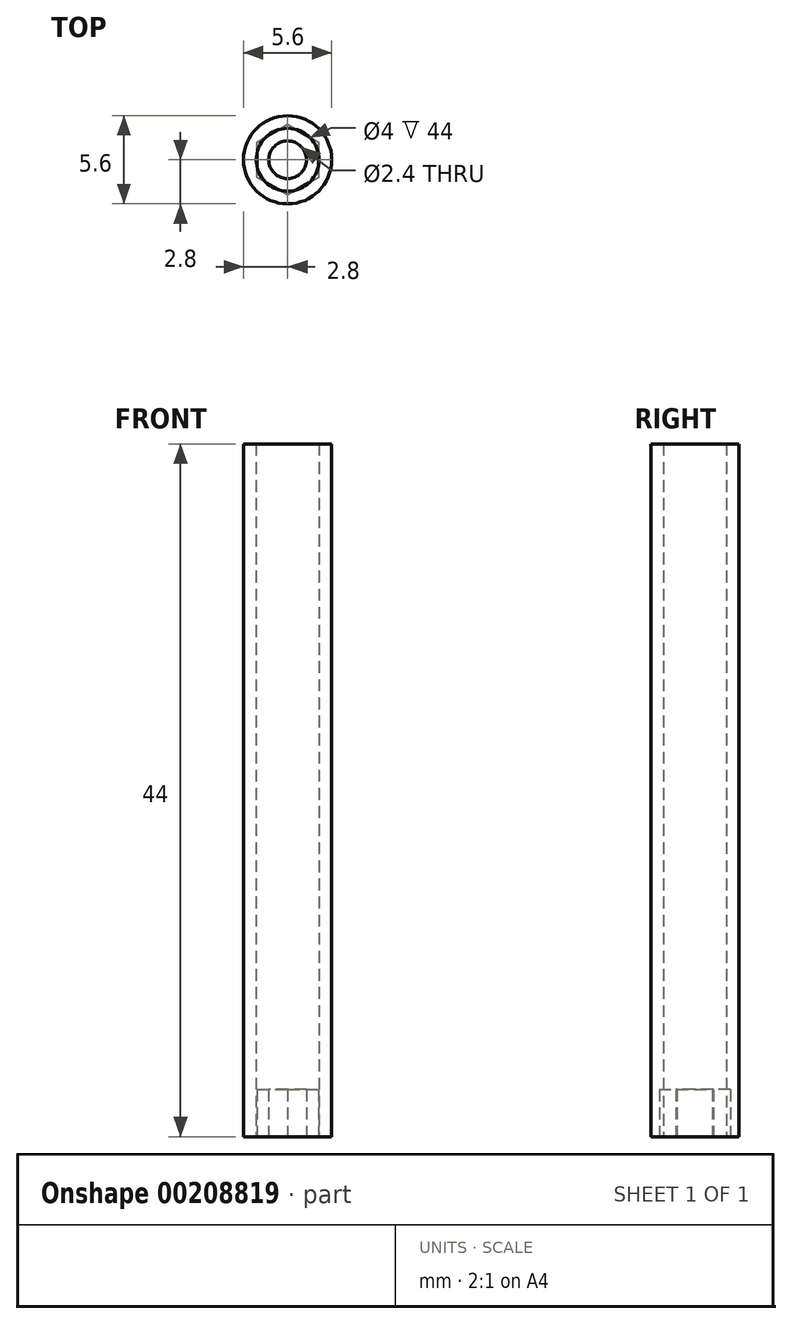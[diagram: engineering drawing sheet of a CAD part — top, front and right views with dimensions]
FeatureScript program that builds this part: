
annotation { "Feature Type Name" : "Feature", "Feature Type Description" : "" }
export const myFeature = defineFeature(function(context is Context, id is Id, definition is map)
    precondition{}
    {
        {
            var Q0;
            Q0=qCreatedBy(makeId("Top.planeOp"),FACE);
            var sketch = newSketch(context, id + "F0", { "sketchPlane" : qUnion([Q0])});
            skCircle(sketch, "E0", {"center": v(0, 0) * mm, "radius": 1.2 * mm});
            skCircle(sketch, "E1.cCircle", {"center": v(0, 0) * mm, "radius": 1.95 * mm, "construction": true});
            skLineSegment(sketch, "E1.0", {"start": v(1.95, 1.13) * mm, "end": v(1.95, -1.13) * mm});
            skLineSegment(sketch, "E1.1", {"start": v(1.95, -1.13) * mm, "end": v(0, -2.25) * mm});
            skLineSegment(sketch, "E1.2", {"start": v(0, -2.25) * mm, "end": v(-1.95, -1.13) * mm});
            skLineSegment(sketch, "E1.3", {"start": v(-1.95, -1.13) * mm, "end": v(-1.95, 1.13) * mm});
            skLineSegment(sketch, "E1.4", {"start": v(-1.95, 1.13) * mm, "end": v(0, 2.25) * mm});
            skLineSegment(sketch, "E1.5", {"start": v(0, 2.25) * mm, "end": v(1.95, 1.13) * mm});
            skPoint(sketch, "E1.0.midPoint", {"position": v(1.95, 0) * mm});
            skSolve(sketch);
        }
        {
            var Q0;
            Q0=makeQuery(id+"F0.imprint","IMPRINT",FACE,{"disambiguationData":[TD([[makeQuery(id+"F0.imprint","IMPRINT",EDGE,{"derivedFrom":sQuery(id+"F0.wireOp",EDGE,"E0")}),-1.0]])]});
            extrude(context, id + "F1", {"entities" : qUnion([Q0]), "depth" : 3 * mm});
        }
        {
            var Q0;
            Q0=qCreatedBy(makeId("Top.planeOp"),FACE);
            var sketch = newSketch(context, id + "F2", { "sketchPlane" : qUnion([Q0])});
            skCircle(sketch, "E2", {"center": v(0, 0) * mm, "radius": 2 * mm});
            skCircle(sketch, "E3", {"center": v(0, 0) * mm, "radius": 2.8 * mm});
            skSolve(sketch);
        }
        {
            var Q0;
            Q0=makeQuery(id+"F2.imprint","IMPRINT",FACE,{"disambiguationData":[TD([[makeQuery(id+"F2.imprint","IMPRINT",EDGE,{"derivedFrom":sQuery(id+"F2.wireOp",EDGE,"E2")}),-1.0]])]});
            extrude(context, id + "F3", {"entities" : qUnion([Q0]), "depth" : 44 * mm});
        }
    });
